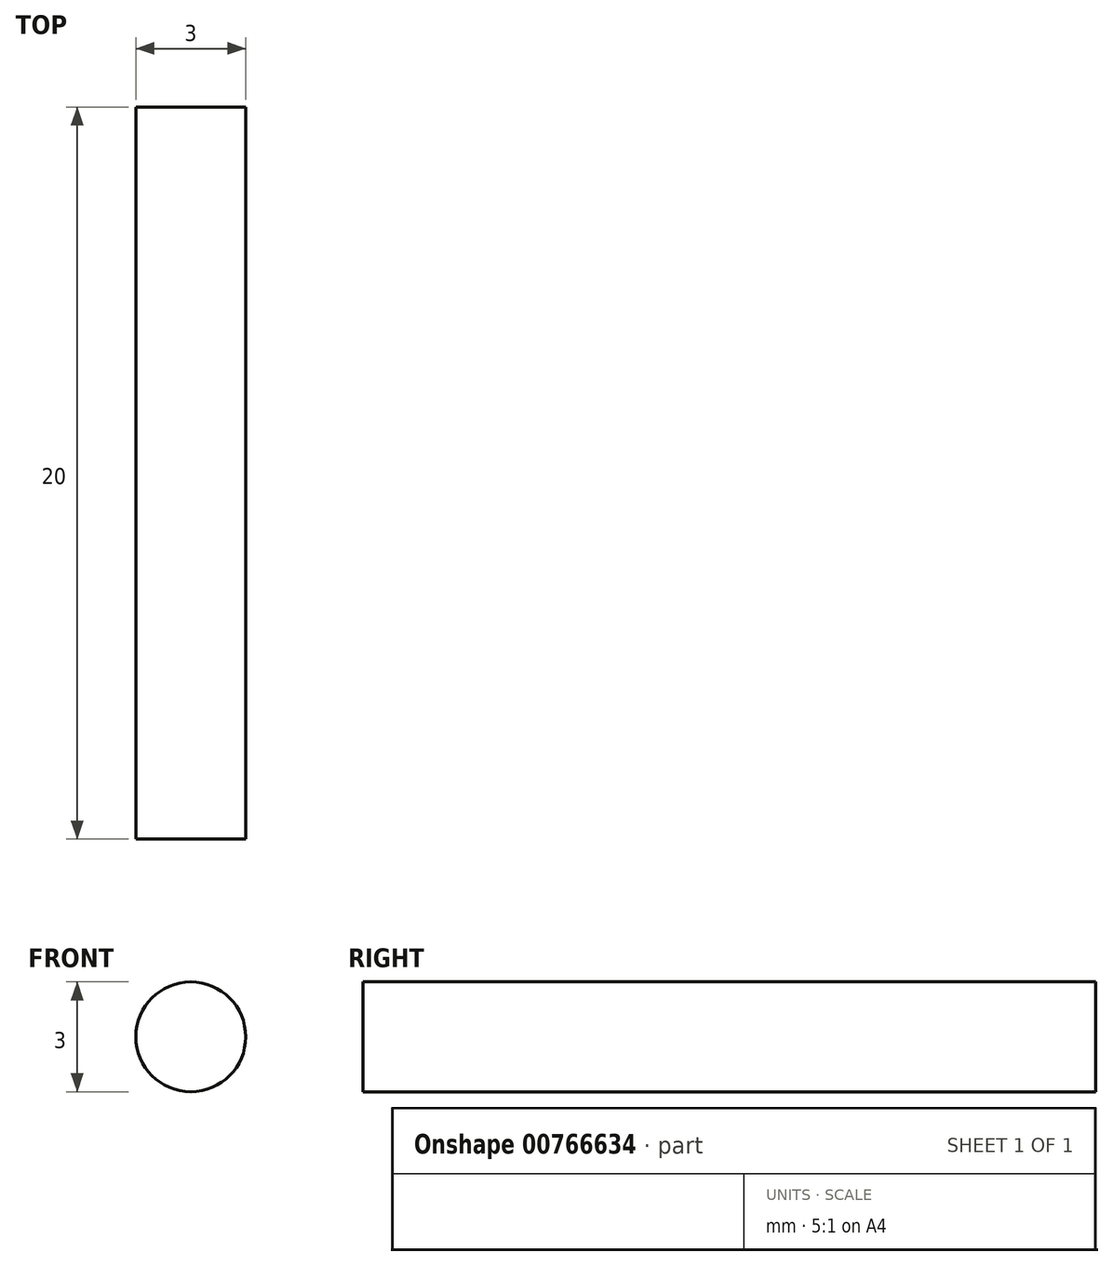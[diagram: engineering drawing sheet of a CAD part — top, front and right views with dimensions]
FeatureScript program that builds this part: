
annotation { "Feature Type Name" : "Feature", "Feature Type Description" : "" }
export const myFeature = defineFeature(function(context is Context, id is Id, definition is map)
    precondition{}
    {
        {
            var Q0;
            Q0=qCreatedBy(makeId("Front.planeOp"),FACE);
            var sketch = newSketch(context, id + "F0", { "sketchPlane" : qUnion([Q0])});
            skCircle(sketch, "E0", {"center": v(0, 0) * mm, "radius": 1.5 * mm});
            skSolve(sketch);
        }
        {
            var Q0;
            Q0=qSketchRegion(id+"F0",true);
            extrude(context, id + "F1", {"entities" : qUnion([Q0]), "depth" : 20 * mm, "offsetDistance" : 25 * mm});
        }
    });
